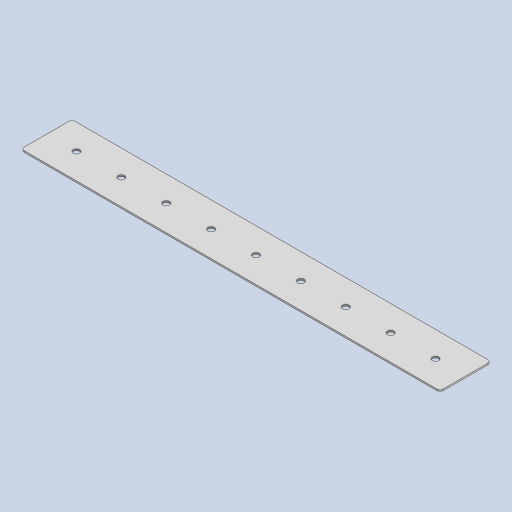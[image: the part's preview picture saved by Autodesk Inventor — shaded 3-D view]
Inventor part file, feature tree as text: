
AUTODESK INVENTOR PART (.ipt)
format: ipt  version: 2023 (Build 270158000, 158)  size: 112,128 bytes
history: native  units: in
note: dims shown in document units (in); Inventor stores cm internally (conversion verified against a paired STEP export)
features: other x1, extrude x1, fillet x1, sketch x1
ambient origin geometry x8: Origin, YZ Plane, XZ Plane, XY Plane, X Axis, Y Axis, Z Axis, Center Point
bodies: Body1 (feature_tree)
feature tree (4):
  other  "ソリッド1"
  extrude  "押し出し1"  Depth=5.5118in
  fillet  "フィレット1"  Radius=0.6693in
  sketch  "スケッチ1"
